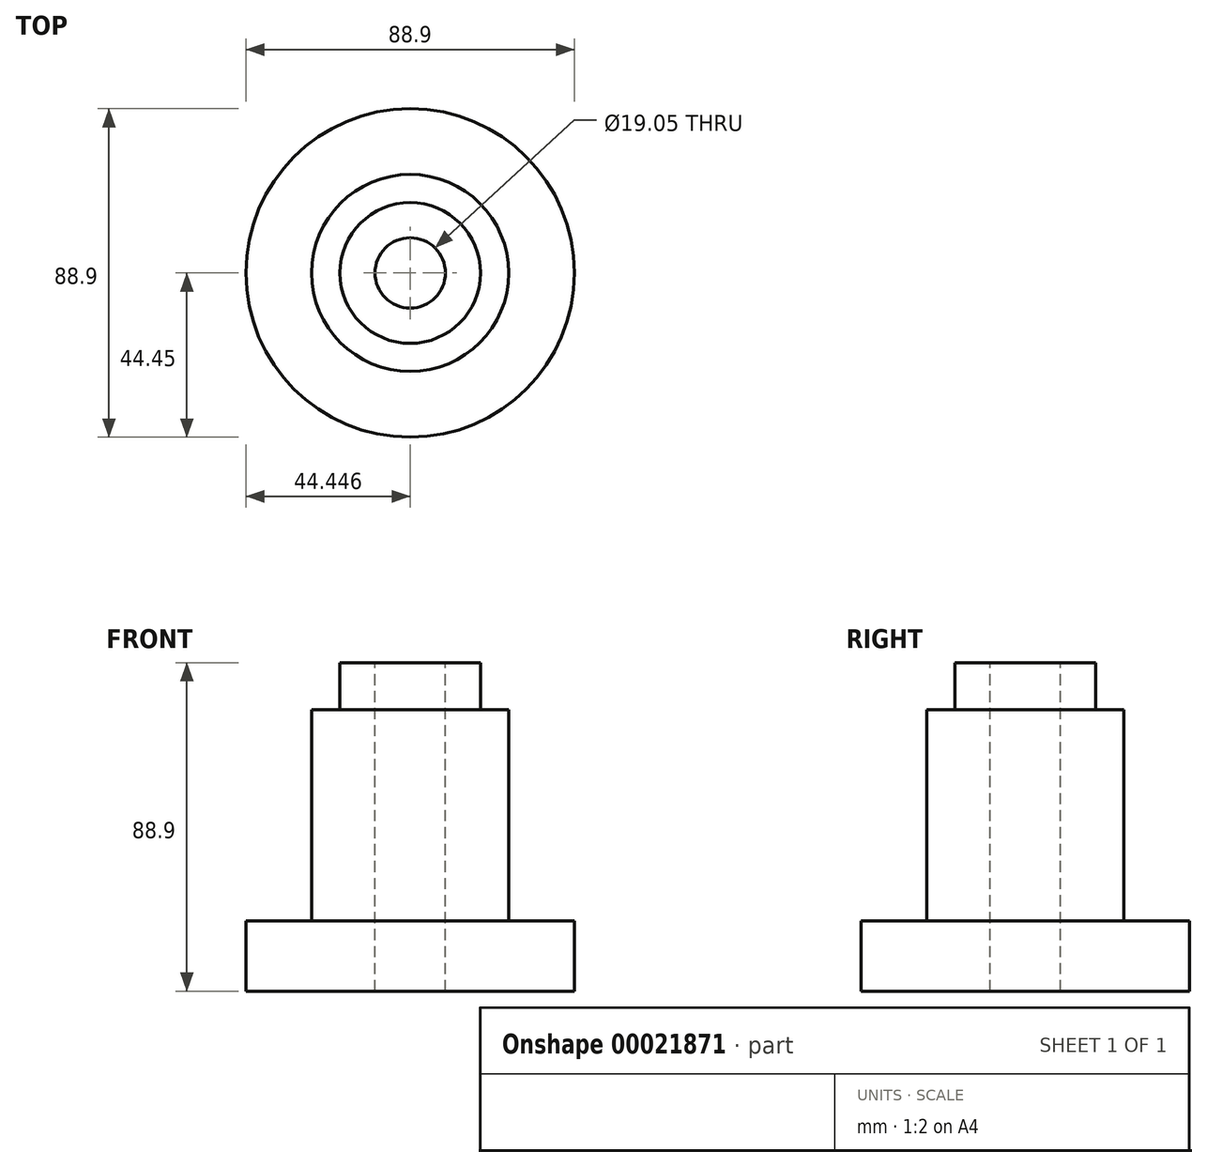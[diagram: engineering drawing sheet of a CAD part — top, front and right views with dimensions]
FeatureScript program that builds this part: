
annotation { "Feature Type Name" : "Feature", "Feature Type Description" : "" }
export const myFeature = defineFeature(function(context is Context, id is Id, definition is map)
    precondition{}
    {
        {
            var Q0;
            Q0=qCreatedBy(makeId("Front.planeOp"),FACE);
            var sketch = newSketch(context, id + "F0", { "sketchPlane" : qUnion([Q0])});
            skLineSegment(sketch, "E0", {"start": v(-35.17, -51.23) * mm, "end": v(-0.24, -51.23) * mm});
            skLineSegment(sketch, "E1", {"start": v(-0.24, -51.23) * mm, "end": v(-0.24, -32.18) * mm});
            skLineSegment(sketch, "E2", {"start": v(-0.24, -32.18) * mm, "end": v(-18.02, -32.18) * mm});
            skLineSegment(sketch, "E3", {"start": v(-18.02, -32.18) * mm, "end": v(-18.02, 24.97) * mm});
            skLineSegment(sketch, "E4", {"start": v(-18.02, 24.97) * mm, "end": v(-25.64, 24.97) * mm});
            skLineSegment(sketch, "E5", {"start": v(-25.64, 24.97) * mm, "end": v(-25.64, 37.67) * mm});
            skLineSegment(sketch, "E6", {"start": v(-25.64, 37.67) * mm, "end": v(-35.17, 37.67) * mm});
            skLineSegment(sketch, "E7", {"start": v(-35.17, 37.67) * mm, "end": v(-35.17, -51.23) * mm});
            skLineSegment(sketch, "E8", {"start": v(-44.7, 36.6) * mm, "end": v(-44.7, -52.3) * mm});
            skSolve(sketch);
        }
        {
            var Q0;
            Q0=makeQuery(id+"F0.imprint","IMPRINT",FACE,{"disambiguationData":[TD([[makeQuery(id+"F0.imprint","IMPRINT",EDGE,{"derivedFrom":sQuery(id+"F0.wireOp",EDGE,"E0")}),1.0]])]});
            var Q1;
            Q1=sQuery(id+"F0.wireOp",EDGE,"E8");
            revolve(context, id + "F1", {"entities" : qUnion([Q0]), "axis" : qUnion([Q1]), "revolveType" : RevolveType.FULL});
        }
    });
